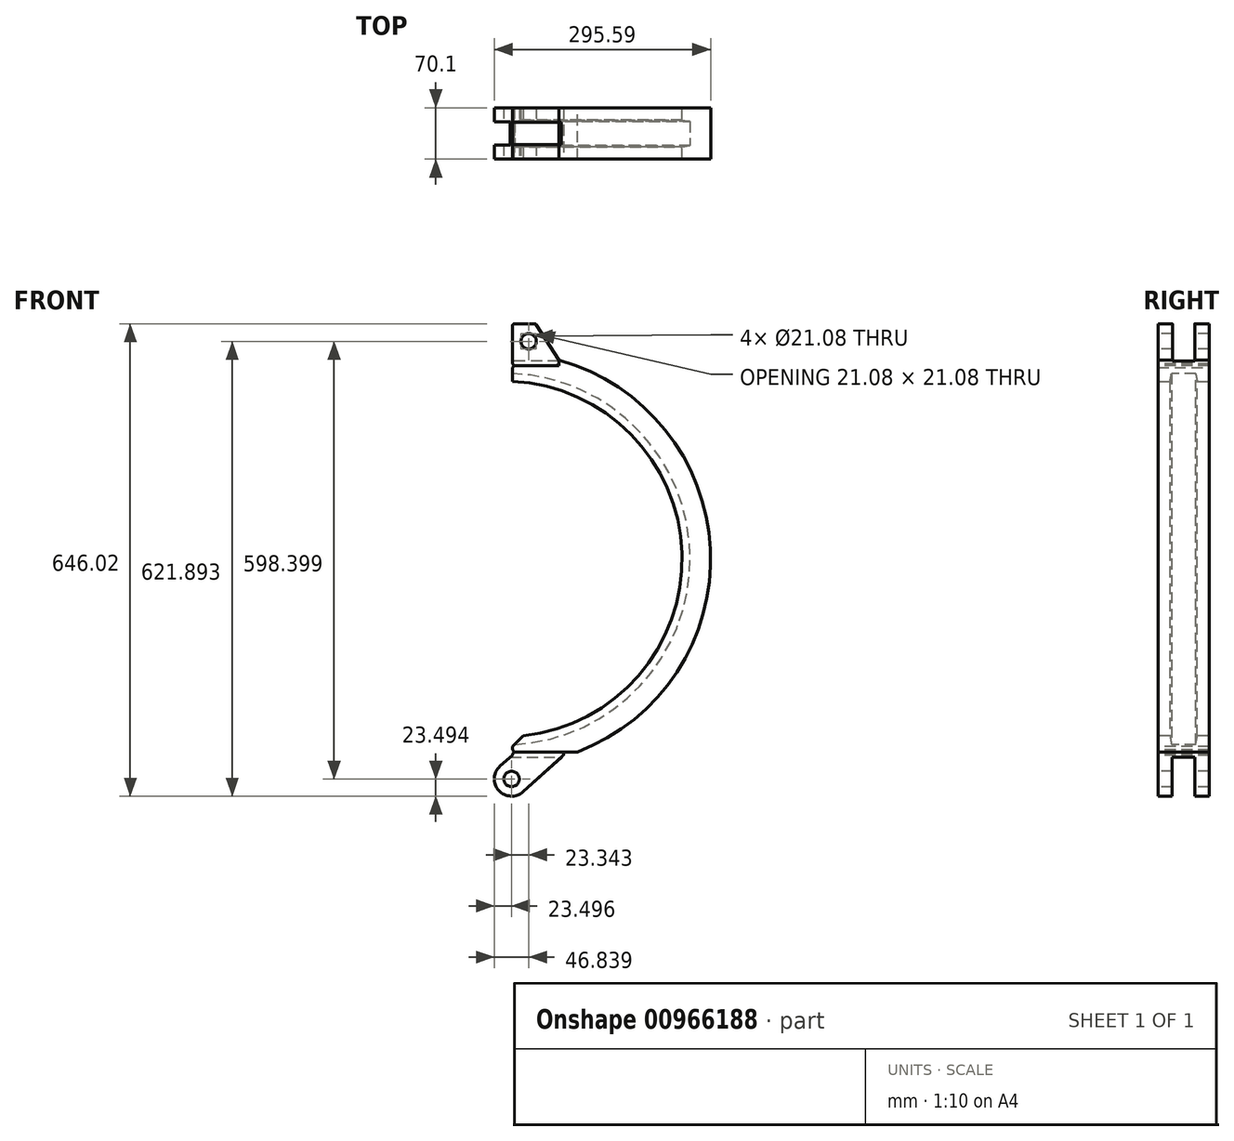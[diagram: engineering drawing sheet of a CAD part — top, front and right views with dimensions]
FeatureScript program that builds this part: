
annotation { "Feature Type Name" : "Feature", "Feature Type Description" : "" }
export const myFeature = defineFeature(function(context is Context, id is Id, definition is map)
    precondition{}
    {
        {
            var Q0;
            Q0=qCreatedBy(makeId("Front.planeOp"),FACE);
            var sketch = newSketch(context, id + "F0", { "sketchPlane" : qUnion([Q0])});
            skArc(sketch, "E0", {"start": v(11.02, -281.79) * mm, "mid": v(282, 0) * mm, "end": v(11.02, 281.79) * mm});
            skArc(sketch, "E1", {"start": v(11.02, -242.75) * mm, "mid": v(243, 0) * mm, "end": v(11.02, 242.75) * mm});
            skLineSegment(sketch, "E2", {"start": v(11.02, 281.79) * mm, "end": v(11.02, 242.75) * mm});
            skLineSegment(sketch, "E3.trimOffspring", {"start": v(11.02, -242.75) * mm, "end": v(11.02, -281.79) * mm});
            skSolve(sketch);
        }
        {
            var Q0;
            Q0=makeQuery(id+"F0.imprint","IMPRINT",FACE,{"disambiguationData":[TD([[makeQuery(id+"F0.imprint","IMPRINT",EDGE,{"derivedFrom":sQuery(id+"F0.wireOp",EDGE,"E0")}),1.0]])]});
            extrude(context, id + "F1", {"entities" : qUnion([Q0]), "depth" : 70.1 * mm, "offsetDistance" : 25.4 * mm});
        }
        {
            var Q0;
            Q0=makeQuery(id+"F1.opExtrude","SWEPT_FACE",FACE,{"disambiguationData":[OSD([sQuery(id+"F0.wireOp",EDGE,"E2")])]});
            var sketch = newSketch(context, id + "F2", { "sketchPlane" : qUnion([Q0])});
            skLineSegment(sketch, "E4", {"start": v(16.4, 242.75) * mm, "end": v(18.52, 253.68) * mm});
            skLineSegment(sketch, "E5", {"start": v(18.52, 253.68) * mm, "end": v(51.58, 253.68) * mm});
            skLineSegment(sketch, "E6", {"start": v(51.58, 253.68) * mm, "end": v(53.7, 242.75) * mm});
            skSolve(sketch);
        }
        {
            var Q0;
            {var subQ0=sQuery(id+"F2.wireOp",EDGE,"E4");Q0=makeQuery(id+"F2.imprint","IMPRINT",FACE,{"disambiguationData":[TD([[makeQuery(id+"F2.imprint","IMPRINT",EDGE,{"derivedFrom":subQ0}),-1.0]])]});}
            var Q1;
            Q1=makeQuery(id+"F1.opExtrude","CAP_EDGE",EDGE,{"disambiguationData":[OSD([sQuery(id+"F0.wireOp",EDGE,"E1")])],"isStart":false});
            revolve(context, id + "F3", {"operationType" : NewBodyOperationType.REMOVE, "surfaceOperationType" : NewSurfaceOperationType.NEW, "entities" : qUnion([Q0]), "axis" : qUnion([Q1]), "revolveType" : RevolveType.FULL, "oppositeDirection" : true});
        }
        {
            var Q0;
            Q0=makeQuery(id+"F1.opExtrude","CAP_FACE",FACE,{"disambiguationData":[OSD([sQuery(id+"F0.wireOp",EDGE,"E0"),sQuery(id+"F0.wireOp",EDGE,"E1"),sQuery(id+"F0.wireOp",EDGE,"E2"),sQuery(id+"F0.wireOp",EDGE,"E3.trimOffspring")])],"isStart":false});
            var sketch = newSketch(context, id + "F4", { "sketchPlane" : qUnion([Q0])});
            skLineSegment(sketch, "E7.bottom", {"start": v(-35.17, 300.6) * mm, "end": v(74.52, 300.6) * mm});
            skLineSegment(sketch, "E7.top", {"start": v(-35.17, 264.64) * mm, "end": v(74.52, 264.64) * mm});
            skLineSegment(sketch, "E7.left", {"start": v(-35.17, 300.6) * mm, "end": v(-35.17, 264.64) * mm});
            skLineSegment(sketch, "E7.right", {"start": v(74.52, 300.6) * mm, "end": v(74.52, 264.64) * mm});
            skLineSegment(sketch, "E8.bottom", {"start": v(-25.4, -263.65) * mm, "end": v(152.3, -263.65) * mm});
            skLineSegment(sketch, "E8.top", {"start": v(-25.4, -309.81) * mm, "end": v(152.3, -309.81) * mm});
            skLineSegment(sketch, "E8.left", {"start": v(-25.4, -263.65) * mm, "end": v(-25.4, -309.81) * mm});
            skLineSegment(sketch, "E8.right", {"start": v(152.3, -263.65) * mm, "end": v(152.3, -309.81) * mm});
            skSolve(sketch);
        }
        {
            var Q0;
            Q0=qSketchRegion(id+"F4",true);
            extrude(context, id + "F5", {"entities" : qUnion([Q0]), "operationType" : NewBodyOperationType.REMOVE, "endBound" : BoundingType.THROUGH_ALL, "oppositeDirection" : true, "depth" : 25.4 * mm, "offsetDistance" : 25.4 * mm});
        }
        {
            var Q0;
            Q0=makeQuery(id+"F1.opExtrude","SWEPT_FACE",FACE,{"disambiguationData":[OSD([sQuery(id+"F0.wireOp",EDGE,"E2")])]});
            var sketch = newSketch(context, id + "F6", { "sketchPlane" : qUnion([Q0])});
            skLineSegment(sketch, "E9.bottom", {"start": v(4.83, 264.64) * mm, "end": v(65.28, 264.64) * mm});
            skLineSegment(sketch, "E9.top", {"start": v(4.83, 315.7) * mm, "end": v(65.28, 315.7) * mm});
            skLineSegment(sketch, "E9.left", {"start": v(4.83, 264.64) * mm, "end": v(4.83, 315.7) * mm});
            skLineSegment(sketch, "E9.right", {"start": v(65.28, 264.64) * mm, "end": v(65.28, 315.7) * mm});
            skSolve(sketch);
        }
        {
            var Q0;
            Q0=qSketchRegion(id+"F6",true);
            extrude(context, id + "F7", {"entities" : qUnion([Q0]), "oppositeDirection" : true, "depth" : 59.94 * mm, "offsetDistance" : 25.4 * mm});
        }
        {
            var Q0;
            Q0=makeQuery(id+"F7.boolean.opBoolean","MERGE",FACE,{"derivedFrom":[makeQuery(id+"F1.opExtrude","SWEPT_FACE",FACE,{"disambiguationData":[OSD([sQuery(id+"F0.wireOp",EDGE,"E2")])]}),makeQuery(id+"F7.opExtrude","CAP_FACE",FACE,{"disambiguationData":[OSD([sQuery(id+"F6.wireOp",EDGE,"E9.bottom"),sQuery(id+"F6.wireOp",EDGE,"E9.top"),sQuery(id+"F6.wireOp",EDGE,"E9.left"),sQuery(id+"F6.wireOp",EDGE,"E9.right")])],"isStart":true})]});
            var sketch = newSketch(context, id + "F8", { "sketchPlane" : qUnion([Q0])});
            skArc(sketch, "E10", {"start": v(21.59, 299.97) * mm, "mid": v(35.05, 286.51) * mm, "end": v(48.51, 299.97) * mm});
            skPoint(sketch, "E10.centerSnap0", {"position": v(35.05, 253.68) * mm});
            skLineSegment(sketch, "E11", {"start": v(21.59, 299.97) * mm, "end": v(21.59, 315.7) * mm});
            skLineSegment(sketch, "E12", {"start": v(48.51, 299.97) * mm, "end": v(48.51, 315.7) * mm});
            skLineSegment(sketch, "E13", {"start": v(48.51, 315.7) * mm, "end": v(21.59, 315.7) * mm});
            skSolve(sketch);
        }
        {
            var Q0;
            Q0=makeQuery(id+"F8.imprint","IMPRINT",FACE,{"disambiguationData":[TD([[makeQuery(id+"F8.imprint","IMPRINT",EDGE,{"derivedFrom":sQuery(id+"F8.wireOp",EDGE,"E10")}),1.0]])]});
            extrude(context, id + "F9", {"entities" : qUnion([Q0]), "operationType" : NewBodyOperationType.REMOVE, "endBound" : BoundingType.THROUGH_ALL, "oppositeDirection" : true, "depth" : 25.4 * mm, "offsetDistance" : 25.4 * mm});
        }
        {
            var Q0;
            Q0=makeQuery(id+"F7.opExtrude","CAP_FACE",FACE,{"disambiguationData":[OSD([sQuery(id+"F6.wireOp",EDGE,"E9.bottom"),sQuery(id+"F6.wireOp",EDGE,"E9.top"),sQuery(id+"F6.wireOp",EDGE,"E9.left"),sQuery(id+"F6.wireOp",EDGE,"E9.right")])],"isStart":false});
            var sketch = newSketch(context, id + "F10", { "sketchPlane" : qUnion([Q0])});
            skCircle(sketch, "E14", {"center": v(-35.05, 299.97) * mm, "radius": 20.96 * mm});
            skSolve(sketch);
        }
        {
            var Q0;
            Q0=qSketchRegion(id+"F10",true);
            extrude(context, id + "F11", {"entities" : qUnion([Q0]), "operationType" : NewBodyOperationType.REMOVE, "oppositeDirection" : true, "depth" : 2.54 * mm, "offsetDistance" : 25.4 * mm});
        }
        {
            var Q0;
            Q0=qCreatedBy(makeId("Front.planeOp"),FACE);
            cPlane(context, id + "F12", {"entities" : qUnion([Q0]), "cplaneType" : CPlaneType.OFFSET, "offset" : 35.05 * mm, "width" : 152.4 * mm, "height" : 152.4 * mm});
        }
        {
            var Q0;
            Q0=makeQuery(id+"F1.opExtrude","CAP_FACE",FACE,{"disambiguationData":[OSD([sQuery(id+"F0.wireOp",EDGE,"E0"),sQuery(id+"F0.wireOp",EDGE,"E1"),sQuery(id+"F0.wireOp",EDGE,"E2"),sQuery(id+"F0.wireOp",EDGE,"E3.trimOffspring")])],"isStart":false});
            var sketch = newSketch(context, id + "F13", { "sketchPlane" : qUnion([Q0])});
            skLineSegment(sketch, "E15", {"start": v(78.3, -270.76) * mm, "end": v(25.63, -318.2) * mm});
            skLineSegment(sketch, "E16", {"start": v(-5.82, -283.28) * mm, "end": v(11.02, -268.11) * mm});
            skCircle(sketch, "E17", {"center": v(9.9, -300.74) * mm, "radius": 10.54 * mm});
            skLineSegment(sketch, "E18", {"start": v(0, 0) * mm, "end": v(0, -72.6) * mm, "construction": true});
            skLineSegment(sketch, "E19", {"start": v(9.9, -300.74) * mm, "end": v(-19.12, -326.87) * mm, "construction": true});
            skArc(sketch, "E20", {"start": v(-5.82, -283.28) * mm, "mid": v(-7.55, -316.46) * mm, "end": v(25.63, -318.2) * mm});
            skLineSegment(sketch, "E21", {"start": v(11.02, -266.6) * mm, "end": v(13.96, -263.65) * mm});
            skLineSegment(sketch, "E22", {"start": v(13.96, -263.65) * mm, "end": v(86.2, -263.65) * mm});
            skLineSegment(sketch, "E23", {"start": v(78.3, -270.76) * mm, "end": v(86.2, -263.65) * mm});
            skLineSegment(sketch, "E24", {"start": v(11.02, -266.6) * mm, "end": v(11.02, -268.11) * mm});
            skPoint(sketch, "E25.orphan", {"position": v(15.98, -263.65) * mm});
            skSolve(sketch);
        }
        {
            var Q0;
            Q0=qCreatedBy(id+"F12.planeOp",FACE);
            var sketch = newSketch(context, id + "F14", { "sketchPlane" : qUnion([Q0])});
            skLineSegment(sketch, "E26", {"start": v(78.3, -270.76) * mm, "end": v(25.63, -318.2) * mm});
            skLineSegment(sketch, "E27", {"start": v(-5.82, -283.28) * mm, "end": v(8.08, -270.76) * mm});
            skLineSegment(sketch, "E28", {"start": v(8.08, -270.76) * mm, "end": v(11.02, -270.76) * mm});
            skCircle(sketch, "E29", {"center": v(9.9, -300.74) * mm, "radius": 10.54 * mm});
            skLineSegment(sketch, "E30", {"start": v(0, 0) * mm, "end": v(0, -72.6) * mm, "construction": true});
            skLineSegment(sketch, "E31", {"start": v(9.9, -300.74) * mm, "end": v(-19.12, -326.87) * mm, "construction": true});
            skArc(sketch, "E32", {"start": v(-5.82, -283.28) * mm, "mid": v(-7.55, -316.46) * mm, "end": v(25.63, -318.2) * mm});
            skLineSegment(sketch, "E33", {"start": v(11.02, -270.76) * mm, "end": v(78.3, -270.76) * mm});
            skSolve(sketch);
        }
        {
            var Q0;
            Q0 = qSketchRegion(id + "F13", true);
            extrude(context, id + "F15", {"entities" : qUnion([Q0]), "oppositeDirection" : true, "depth" : 70.1 * mm, "offsetDistance" : 25.4 * mm});
        }
        {
            var Q0;
            Q0=makeQuery(id+"F1.opExtrude","CAP_FACE",FACE,{"disambiguationData":[OSD([sQuery(id+"F0.wireOp",EDGE,"E0"),sQuery(id+"F0.wireOp",EDGE,"E1"),sQuery(id+"F0.wireOp",EDGE,"E2"),sQuery(id+"F0.wireOp",EDGE,"E3.trimOffspring")])],"isStart":false});
            var sketch = newSketch(context, id + "F16", { "sketchPlane" : qUnion([Q0])});
            skLineSegment(sketch, "E34", {"start": v(11.02, -256.6) * mm, "end": v(26, -241.6) * mm});
            skLineSegment(sketch, "E35", {"start": v(11.02, -256.6) * mm, "end": v(11.02, -242.75) * mm});
            skArc(sketch, "E36", {"start": v(11.02, -242.75) * mm, "mid": v(18.53, -242.3) * mm, "end": v(26, -241.6) * mm});
            skLineSegment(sketch, "E37", {"start": v(13.96, -263.65) * mm, "end": v(11.02, -260.71) * mm});
            skLineSegment(sketch, "E38", {"start": v(11.02, -260.71) * mm, "end": v(11.02, -263.65) * mm});
            skLineSegment(sketch, "E39", {"start": v(11.02, -263.65) * mm, "end": v(13.96, -263.65) * mm});
            skSolve(sketch);
        }
        {
            var Q0;
            Q0=qSketchRegion(id+"F16",true);
            extrude(context, id + "F17", {"entities" : qUnion([Q0]), "operationType" : NewBodyOperationType.REMOVE, "endBound" : BoundingType.THROUGH_ALL, "oppositeDirection" : true, "depth" : 25.4 * mm, "offsetDistance" : 25.4 * mm});
        }
        {
            var Q0;
            Q0=makeQuery(id+"F7.opExtrude","SWEPT_BODY",BODY,{"disambiguationData":[OSD([sQuery(id+"F6.wireOp",EDGE,"E9.bottom"),sQuery(id+"F6.wireOp",EDGE,"E9.top"),sQuery(id+"F6.wireOp",EDGE,"E9.left"),sQuery(id+"F6.wireOp",EDGE,"E9.right")])]});
            deleteBodies(context, id + "F18", {"entities" : qUnion([Q0])});
        }
        {
            var Q0;
            Q0 = qSketchRegion(id + "F14", true);
            extrude(context, id + "F19", {"entities" : qUnion([Q0]), "operationType" : NewBodyOperationType.REMOVE, "endBound" : BoundingType.SYMMETRIC, "oppositeDirection" : true, "depth" : 31.24 * mm, "offsetDistance" : 25.4 * mm});
        }
        {
            var Q0;
            Q0=makeQuery(id+"F15.opExtrude","SWEPT_EDGE",EDGE,{"disambiguationData":[OSD([sQuery(id+"F4.wireOp",EDGE,"E8.bottom"),sQuery(id+"F13.wireOp",EDGE,"E22"),sQuery(id+"F13.wireOp",EDGE,"E23")])]});
            fillet(context, id + "F20", {"entities" : qUnion([Q0]), "radius" : 3.17 * mm, "tangentPropagation" : true, "allowEdgeOverflow" : false});
        }
        {
            var Q0;
            Q0=makeQuery(id+"F1.opExtrude","CAP_FACE",FACE,{"disambiguationData":[OSD([sQuery(id+"F0.wireOp",EDGE,"E0"),sQuery(id+"F0.wireOp",EDGE,"E1"),sQuery(id+"F0.wireOp",EDGE,"E2"),sQuery(id+"F0.wireOp",EDGE,"E3.trimOffspring")])],"isStart":false});
            var sketch = newSketch(context, id + "F21", { "sketchPlane" : qUnion([Q0])});
            skLineSegment(sketch, "E40", {"start": v(11.02, 264.64) * mm, "end": v(11.02, 318.62) * mm});
            skLineSegment(sketch, "E41", {"start": v(14.2, 321.8) * mm, "end": v(41.03, 321.8) * mm});
            skLineSegment(sketch, "E42", {"start": v(74.52, 271.98) * mm, "end": v(74.52, 264.64) * mm});
            skLineSegment(sketch, "E43", {"start": v(74.52, 264.64) * mm, "end": v(11.02, 264.64) * mm});
            skLineSegment(sketch, "E44", {"start": v(74.52, 271.98) * mm, "end": v(43.7, 320.32) * mm});
            skPoint(sketch, "E45.orphan", {"position": v(74.52, 321.8) * mm});
            skPoint(sketch, "E46.visualSharp", {"position": v(11.02, 321.8) * mm});
            skArc(sketch, "E46.filletArc", {"start": v(14.2, 321.8) * mm, "mid": v(11.95, 320.86) * mm, "end": v(11.02, 318.62) * mm});
            skPoint(sketch, "E47.visualSharp", {"position": v(42.77, 321.8) * mm});
            skArc(sketch, "E47.filletArc", {"start": v(43.7, 320.32) * mm, "mid": v(42.56, 321.4) * mm, "end": v(41.03, 321.8) * mm});
            skCircle(sketch, "E48", {"center": v(33.25, 297.66) * mm, "radius": 10.54 * mm});
            skSolve(sketch);
        }
        {
            var Q0;
            Q0 = qSketchRegion(id + "F21", true);
            var Q1;
            Q1=makeQuery(id+"F1.opExtrude","CAP_FACE",FACE,{"disambiguationData":[OSD([sQuery(id+"F0.wireOp",EDGE,"E0"),sQuery(id+"F0.wireOp",EDGE,"E1"),sQuery(id+"F0.wireOp",EDGE,"E2"),sQuery(id+"F0.wireOp",EDGE,"E3.trimOffspring")])],"isStart":true});
            extrude(context, id + "F22", {"entities" : qUnion([Q0]), "endBound" : BoundingType.UP_TO_SURFACE, "oppositeDirection" : true, "depth" : 25.4 * mm, "endBoundEntityFace" : qUnion([Q1]), "offsetDistance" : 25.4 * mm});
        }
        {
            var Q0;
            Q0=makeQuery(id+"F22.opExtrude","SWEPT_EDGE",EDGE,{"disambiguationData":[OSD([sQuery(id+"F0.wireOp",EDGE,"E2"),sQuery(id+"F21.wireOp",EDGE,"E40"),sQuery(id+"F21.wireOp",EDGE,"E43")])]});
            chamfer(context, id + "F23", {"entities" : qUnion([Q0]), "width" : 2.54 * mm, "tangentPropagation" : true});
        }
        {
            var Q0;
            Q0=makeQuery(id+"F22.opExtrude","SWEPT_EDGE",EDGE,{"disambiguationData":[OSD([sQuery(id+"F21.wireOp",EDGE,"E42"),sQuery(id+"F21.wireOp",EDGE,"E43")])]});
            fillet(context, id + "F24", {"entities" : qUnion([Q0]), "radius" : 3.17 * mm, "tangentPropagation" : true, "allowEdgeOverflow" : false});
        }
        {
            var Q0;
            Q0=makeQuery(id+"F22.opExtrude","SWEPT_FACE",FACE,{"disambiguationData":[OSD([sQuery(id+"F21.wireOp",EDGE,"E40")])]});
            var sketch = newSketch(context, id + "F25", { "sketchPlane" : qUnion([Q0])});
            skLineSegment(sketch, "E49.bottom", {"start": v(19.81, 321.8) * mm, "end": v(50.3, 321.8) * mm});
            skLineSegment(sketch, "E49.top", {"start": v(19.81, 271) * mm, "end": v(50.3, 271) * mm});
            skLineSegment(sketch, "E49.left", {"start": v(19.81, 321.8) * mm, "end": v(19.81, 271) * mm});
            skLineSegment(sketch, "E49.right", {"start": v(50.3, 321.8) * mm, "end": v(50.3, 271) * mm});
            skSolve(sketch);
        }
        {
            var Q0;
            Q0 = qSketchRegion(id + "F25", true);
            extrude(context, id + "F26", {"entities" : qUnion([Q0]), "operationType" : NewBodyOperationType.REMOVE, "endBound" : BoundingType.THROUGH_ALL, "oppositeDirection" : true, "depth" : 25.4 * mm, "offsetDistance" : 25.4 * mm});
        }
        {
            var Q0;
            Q0=makeQuery(id+"F5.boolean.opBoolean","INTERSECT",EDGE,{"derivedFrom":[makeQuery(id+"F1.opExtrude","SWEPT_FACE",FACE,{"disambiguationData":[OSD([sQuery(id+"F0.wireOp",EDGE,"E2")])]}),makeQuery(id+"F5.opExtrude","SWEPT_FACE",FACE,{"disambiguationData":[OSD([sQuery(id+"F4.wireOp",EDGE,"E7.top")])]})]});
            chamfer(context, id + "F27", {"entities" : qUnion([Q0]), "width" : 2.54 * mm, "tangentPropagation" : true});
        }
    });
